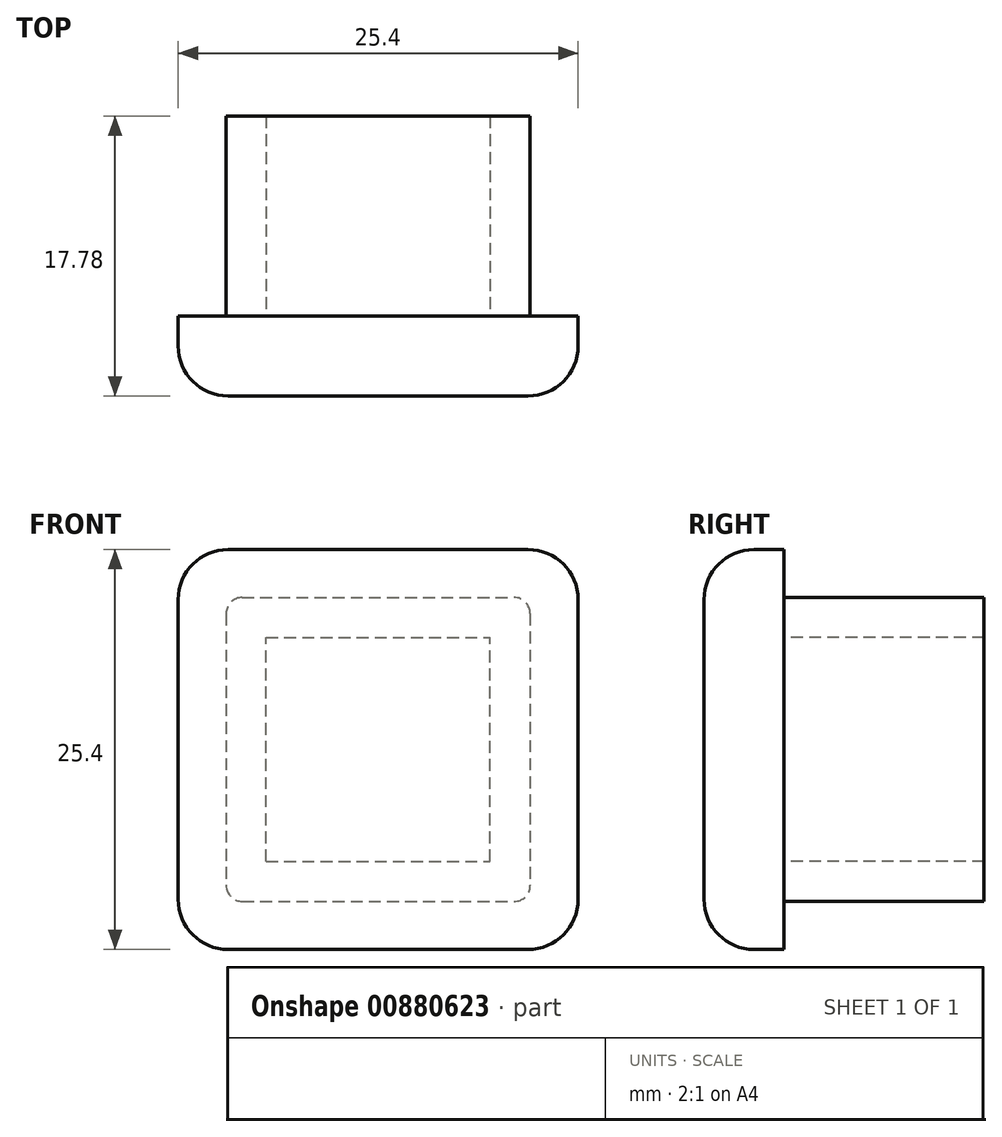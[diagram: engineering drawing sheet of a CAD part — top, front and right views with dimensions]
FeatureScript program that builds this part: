
annotation { "Feature Type Name" : "Feature", "Feature Type Description" : "" }
export const myFeature = defineFeature(function(context is Context, id is Id, definition is map)
    precondition{}
    {
        {
            var Q0;
            Q0=qCreatedBy(makeId("Front.planeOp"),FACE);
            var sketch = newSketch(context, id + "F0", { "sketchPlane" : qUnion([Q0])});
            skLineSegment(sketch, "E0.bottom", {"start": v(-9.53, 12.7) * mm, "end": v(9.52, 12.7) * mm});
            skLineSegment(sketch, "E0.top", {"start": v(-9.53, -12.7) * mm, "end": v(9.52, -12.7) * mm});
            skLineSegment(sketch, "E0.left", {"start": v(-12.7, 9.52) * mm, "end": v(-12.7, -9.53) * mm});
            skLineSegment(sketch, "E0.right", {"start": v(12.7, 9.53) * mm, "end": v(12.7, -9.53) * mm});
            skPoint(sketch, "E1.visualSharp", {"position": v(12.7, 12.7) * mm});
            skArc(sketch, "E1.filletArc", {"start": v(12.7, 9.53) * mm, "mid": v(11.77, 11.77) * mm, "end": v(9.52, 12.7) * mm});
            skPoint(sketch, "E2.visualSharp", {"position": v(12.7, -12.7) * mm});
            skArc(sketch, "E2.filletArc", {"start": v(9.52, -12.7) * mm, "mid": v(11.77, -11.77) * mm, "end": v(12.7, -9.53) * mm});
            skPoint(sketch, "E3.visualSharp", {"position": v(-12.7, -12.7) * mm});
            skArc(sketch, "E3.filletArc", {"start": v(-12.7, -9.53) * mm, "mid": v(-11.77, -11.77) * mm, "end": v(-9.53, -12.7) * mm});
            skPoint(sketch, "E4.visualSharp", {"position": v(-12.7, 12.7) * mm});
            skArc(sketch, "E4.filletArc", {"start": v(-9.53, 12.7) * mm, "mid": v(-11.77, 11.77) * mm, "end": v(-12.7, 9.52) * mm});
            skLineSegment(sketch, "E5", {"start": v(0, 12.7) * mm, "end": v(0, 0) * mm, "construction": true});
            skLineSegment(sketch, "E6", {"start": v(0, 0) * mm, "end": v(12.7, 0) * mm, "construction": true});
            skSolve(sketch);
        }
        {
            var Q0;
            Q0 = qSketchRegion(id + "F0", true);
            extrude(context, id + "F1", {"entities" : qUnion([Q0]), "depth" : 5.08 * mm, "offsetDistance" : 25.4 * mm});
        }
        {
            var Q0;
            Q0=makeQuery(id+"F1.opExtrude","CAP_EDGE",EDGE,{"disambiguationData":[OSD([sQuery(id+"F0.wireOp",EDGE,"E0.right")])],"isStart":false});
            fillet(context, id + "F2", {"entities" : qUnion([Q0]), "radius" : 3.17 * mm, "tangentPropagation" : true, "allowEdgeOverflow" : false});
        }
        {
            var Q0;
            Q0=makeQuery(id+"F1.opExtrude","CAP_FACE",FACE,{"disambiguationData":[OSD([sQuery(id+"F0.wireOp",EDGE,"E0.bottom"),sQuery(id+"F0.wireOp",EDGE,"E0.top"),sQuery(id+"F0.wireOp",EDGE,"E0.left"),sQuery(id+"F0.wireOp",EDGE,"E0.right"),sQuery(id+"F0.wireOp",EDGE,"E1.filletArc"),sQuery(id+"F0.wireOp",EDGE,"E2.filletArc"),sQuery(id+"F0.wireOp",EDGE,"E3.filletArc"),sQuery(id+"F0.wireOp",EDGE,"E4.filletArc")])],"isStart":true});
            var sketch = newSketch(context, id + "F3", { "sketchPlane" : qUnion([Q0])});
            skLineSegment(sketch, "E7.bottom", {"start": v(8.64, 9.65) * mm, "end": v(-8.64, 9.65) * mm});
            skLineSegment(sketch, "E7.top", {"start": v(8.64, -9.65) * mm, "end": v(-8.64, -9.65) * mm});
            skLineSegment(sketch, "E7.left", {"start": v(9.65, 8.64) * mm, "end": v(9.65, -8.64) * mm});
            skLineSegment(sketch, "E7.right", {"start": v(-9.65, 8.64) * mm, "end": v(-9.65, -8.64) * mm});
            skPoint(sketch, "E8.visualSharp", {"position": v(9.65, -9.65) * mm});
            skArc(sketch, "E8.filletArc", {"start": v(8.64, -9.65) * mm, "mid": v(9.35, -9.35) * mm, "end": v(9.65, -8.64) * mm});
            skPoint(sketch, "E9.visualSharp", {"position": v(-9.65, -9.65) * mm});
            skArc(sketch, "E9.filletArc", {"start": v(-9.65, -8.64) * mm, "mid": v(-9.35, -9.35) * mm, "end": v(-8.64, -9.65) * mm});
            skPoint(sketch, "E10.visualSharp", {"position": v(-9.65, 9.65) * mm});
            skArc(sketch, "E10.filletArc", {"start": v(-8.64, 9.65) * mm, "mid": v(-9.35, 9.35) * mm, "end": v(-9.65, 8.64) * mm});
            skPoint(sketch, "E11.visualSharp", {"position": v(9.65, 9.65) * mm});
            skArc(sketch, "E11.filletArc", {"start": v(9.65, 8.64) * mm, "mid": v(9.35, 9.35) * mm, "end": v(8.64, 9.65) * mm});
            skLineSegment(sketch, "E12", {"start": v(0, 0) * mm, "end": v(9.65, 0) * mm, "construction": true});
            skLineSegment(sketch, "E13", {"start": v(0, 0) * mm, "end": v(0, -9.65) * mm, "construction": true});
            skSolve(sketch);
        }
        {
            var Q0;
            Q0 = qSketchRegion(id + "F3", true);
            extrude(context, id + "F4", {"entities" : qUnion([Q0]), "operationType" : NewBodyOperationType.ADD, "depth" : 12.7 * mm, "offsetDistance" : 25.4 * mm});
        }
        {
            var Q0;
            Q0=makeQuery(id+"F1.opExtrude","CAP_FACE",FACE,{"disambiguationData":[OSD([sQuery(id+"F0.wireOp",EDGE,"E0.bottom"),sQuery(id+"F0.wireOp",EDGE,"E0.top"),sQuery(id+"F0.wireOp",EDGE,"E0.left"),sQuery(id+"F0.wireOp",EDGE,"E0.right"),sQuery(id+"F0.wireOp",EDGE,"E1.filletArc"),sQuery(id+"F0.wireOp",EDGE,"E2.filletArc"),sQuery(id+"F0.wireOp",EDGE,"E3.filletArc"),sQuery(id+"F0.wireOp",EDGE,"E4.filletArc")])],"isStart":true});
            var sketch = newSketch(context, id + "F5", { "sketchPlane" : qUnion([Q0])});
            skLineSegment(sketch, "E14.bottom", {"start": v(-7.11, 7.11) * mm, "end": v(7.11, 7.11) * mm});
            skLineSegment(sketch, "E14.top", {"start": v(-7.11, -7.11) * mm, "end": v(7.11, -7.11) * mm});
            skLineSegment(sketch, "E14.left", {"start": v(-7.11, 7.11) * mm, "end": v(-7.11, -7.11) * mm});
            skLineSegment(sketch, "E14.right", {"start": v(7.11, 7.11) * mm, "end": v(7.11, -7.11) * mm});
            skSolve(sketch);
        }
        {
            var Q0;
            Q0 = qSketchRegion(id + "F5", true);
            extrude(context, id + "F6", {"entities" : qUnion([Q0]), "operationType" : NewBodyOperationType.REMOVE, "depth" : 43.7 * mm, "offsetDistance" : 25.4 * mm});
        }
    });
